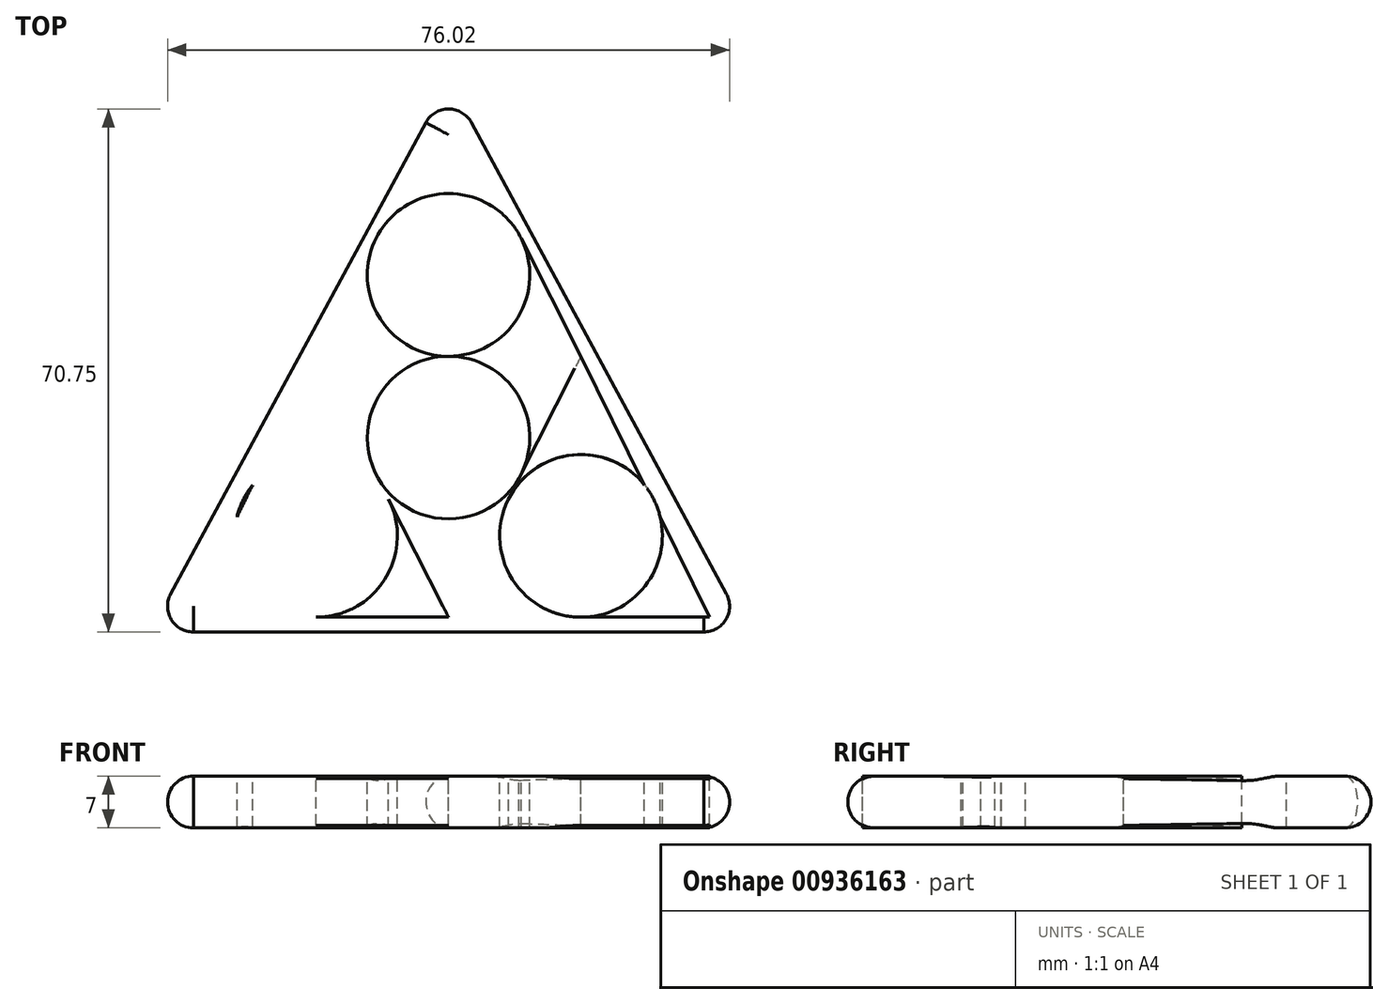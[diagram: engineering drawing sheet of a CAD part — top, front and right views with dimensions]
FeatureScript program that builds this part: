
annotation { "Feature Type Name" : "Feature", "Feature Type Description" : "" }
export const myFeature = defineFeature(function(context is Context, id is Id, definition is map)
    precondition{}
    {
        {
            var Q0;
            Q0=qCreatedBy(makeId("Top.planeOp"),FACE);
            var sketch = newSketch(context, id + "F0", { "sketchPlane" : qUnion([Q0])});
            skLineSegment(sketch, "E0", {"start": v(0, -35.3) * mm, "end": v(-17.92, 0) * mm});
            skLineSegment(sketch, "E1", {"start": v(-17.92, 0) * mm, "end": v(17.92, 0) * mm});
            skLineSegment(sketch, "E2", {"start": v(17.92, 0) * mm, "end": v(0, -35.3) * mm});
            skLineSegment(sketch, "E3", {"start": v(-17.92, 0) * mm, "end": v(-35.3, -35.3) * mm});
            skLineSegment(sketch, "E4", {"start": v(-35.3, -35.3) * mm, "end": v(0, -35.3) * mm});
            skLineSegment(sketch, "E5.MirrorCS", {"start": v(17.92, 0) * mm, "end": v(26.49, -17.4) * mm});
            skLineSegment(sketch, "E6.MirrorCS", {"start": v(35.3, -35.3) * mm, "end": v(0, -35.3) * mm});
            skLineSegment(sketch, "E7", {"start": v(-17.92, 0) * mm, "end": v(0, 35.3) * mm});
            skLineSegment(sketch, "E8", {"start": v(0, 35.3) * mm, "end": v(17.92, 0) * mm});
            skCircle(sketch, "E9", {"center": v(0, -11) * mm, "radius": 11 * mm});
            skPoint(sketch, "E9.centerSnap0", {"position": v(11, -22) * mm});
            skLineSegment(sketch, "E10", {"start": v(0, 35.3) * mm, "end": v(0, 37.3) * mm});
            skLineSegment(sketch, "E11", {"start": v(0, 37.3) * mm, "end": v(-40.39, -37.3) * mm});
            skLineSegment(sketch, "E12", {"start": v(-40.39, -37.3) * mm, "end": v(40.39, -37.3) * mm});
            skLineSegment(sketch, "E13", {"start": v(40.39, -37.3) * mm, "end": v(0, 37.3) * mm});
            skCircle(sketch, "E14", {"center": v(0, 11) * mm, "radius": 11 * mm});
            skPoint(sketch, "E15.center", {"position": v(0, 0) * mm});
            skArc(sketch, "E16.trimOffspring", {"start": v(9.51, -16.56) * mm, "mid": v(9.52, -16.53) * mm, "end": v(9.53, -16.5) * mm});
            skPoint(sketch, "E17", {"position": v(17.92, -24.3) * mm});
            skPoint(sketch, "E18", {"position": v(-17.52, -22.4) * mm});
            skCircle(sketch, "E19", {"center": v(17.92, -24.3) * mm, "radius": 11 * mm});
            skCircle(sketch, "E20.MirrorC", {"center": v(-17.92, -24.3) * mm, "radius": 11 * mm});
            skArc(sketch, "E21.trimOffspring", {"start": v(-10.18, -16.48) * mm, "mid": v(-9.86, -16.5) * mm, "end": v(-9.54, -16.5) * mm});
            skLineSegment(sketch, "E22.trimOffspring", {"start": v(28.61, -21.72) * mm, "end": v(35.3, -35.3) * mm});
            skSolve(sketch);
        }
        {
            var Q0;
            Q0=makeQuery(id+"F0.imprint","IMPRINT",FACE,{"disambiguationData":[TD([[makeQuery(id+"F0.imprint","IMPRINT",EDGE,{"derivedFrom":sQuery(id+"F0.wireOp",EDGE,"E11")}),1.0]])]});
            var Q1;
            {var subQ0=sQuery(id+"F0.wireOp",EDGE,"E8");var subQ1=sQuery(id+"F0.wireOp",EDGE,"E7");var subQ2=makeQuery(id+"F0.imprint","INTERSECT",VERTEX,{"derivedFrom":[subQ1,subQ0]});Q1=makeQuery(id+"F0.imprint","IMPRINT",FACE,{"disambiguationData":[TD([[makeQuery(id+"F0.imprint","IMPRINT",EDGE,{"disambiguationData":[TD([[subQ2,1.0]])],"derivedFrom":subQ1}),-1.0]])]});}
            var Q2;
            {var subQ0=sQuery(id+"F0.wireOp",EDGE,"E4");var subQ1=sQuery(id+"F0.wireOp",EDGE,"E3");var subQ2=makeQuery(id+"F0.imprint","INTERSECT",VERTEX,{"derivedFrom":[subQ1,subQ0]});Q2=makeQuery(id+"F0.imprint","IMPRINT",FACE,{"disambiguationData":[TD([[makeQuery(id+"F0.imprint","IMPRINT",EDGE,{"disambiguationData":[TD([[subQ2,1.0]])],"derivedFrom":subQ1}),1.0]])]});}
            var Q3;
            {var subQ0=sQuery(id+"F0.wireOp",EDGE,"E6.MirrorCS");var subQ1=sQuery(id+"F0.wireOp",EDGE,"E5.MirrorCS");var subQ2=makeQuery(id+"F0.imprint","INTERSECT",VERTEX,{"derivedFrom":[subQ1,subQ0]});Q3=makeQuery(id+"F0.imprint","IMPRINT",FACE,{"disambiguationData":[TD([[makeQuery(id+"F0.imprint","IMPRINT",EDGE,{"disambiguationData":[TD([[subQ2,1.0]])],"derivedFrom":subQ1}),-1.0]])]});}
            var Q4;
            {var subQ0=sQuery(id+"F0.wireOp",EDGE,"E7");var subQ3=sQuery(id+"F0.wireOp",EDGE,"E14");var subQ5=makeQuery(id+"F0.imprint","INTERSECT",VERTEX,{"derivedFrom":[subQ0,subQ3]});Q4=makeQuery(id+"F0.imprint","IMPRINT",FACE,{"disambiguationData":[TD([[makeQuery(id+"F0.imprint","IMPRINT",EDGE,{"disambiguationData":[TD([[subQ5,-1.0]])],"derivedFrom":subQ3}),-1.0]])]});}
            var Q5;
            {var subQ1=sQuery(id+"F0.wireOp",EDGE,"E0");var subQ3=sQuery(id+"F0.wireOp",EDGE,"E20.MirrorC");var subQ4=makeQuery(id+"F0.imprint","INTERSECT",VERTEX,{"derivedFrom":[subQ1,subQ3]});Q5=makeQuery(id+"F0.imprint","IMPRINT",FACE,{"disambiguationData":[TD([[makeQuery(id+"F0.imprint","IMPRINT",EDGE,{"disambiguationData":[TD([[subQ4,-1.0]])],"derivedFrom":subQ3}),1.0]])]});}
            var Q6;
            {var subQ1=sQuery(id+"F0.wireOp",EDGE,"E2");var subQ3=sQuery(id+"F0.wireOp",EDGE,"E19");var subQ4=makeQuery(id+"F0.imprint","INTERSECT",VERTEX,{"derivedFrom":[subQ1,subQ3]});Q6=makeQuery(id+"F0.imprint","IMPRINT",FACE,{"disambiguationData":[TD([[makeQuery(id+"F0.imprint","IMPRINT",EDGE,{"disambiguationData":[TD([[subQ4,-1.0]])],"derivedFrom":subQ3}),-1.0]])]});}
            var Q7;
            {var subQ0=sQuery(id+"F0.wireOp",EDGE,"E21.trimOffspring");Q7=makeQuery(id+"F0.imprint","IMPRINT",FACE,{"disambiguationData":[TD([[makeQuery(id+"F0.imprint","IMPRINT",EDGE,{"derivedFrom":subQ0}),1.0]])]});}
            var Q8;
            {var subQ0=sQuery(id+"F0.wireOp",EDGE,"E21.trimOffspring");Q8=makeQuery(id+"F0.imprint","IMPRINT",FACE,{"disambiguationData":[TD([[makeQuery(id+"F0.imprint","IMPRINT",EDGE,{"derivedFrom":subQ0}),-1.0]])]});}
            var Q9;
            {var subQ0=sQuery(id+"F0.wireOp",EDGE,"E16.trimOffspring");Q9=makeQuery(id+"F0.imprint","IMPRINT",FACE,{"disambiguationData":[TD([[makeQuery(id+"F0.imprint","IMPRINT",EDGE,{"derivedFrom":subQ0}),1.0]])]});}
            var Q10;
            {var subQ1=sQuery(id+"F0.wireOp",EDGE,"E0");var subQ3=sQuery(id+"F0.wireOp",EDGE,"E9");var subQ4=makeQuery(id+"F0.imprint","INTERSECT",VERTEX,{"derivedFrom":[subQ1,subQ3]});Q10=makeQuery(id+"F0.imprint","IMPRINT",FACE,{"disambiguationData":[TD([[makeQuery(id+"F0.imprint","IMPRINT",EDGE,{"disambiguationData":[TD([[subQ4,1.0]])],"derivedFrom":subQ3}),-1.0]])]});}
            var Q11;
            {var subQ1=sQuery(id+"F0.wireOp",EDGE,"E2");var subQ5=makeQuery(id+"F0.imprint","INTERSECT",VERTEX,{"derivedFrom":[subQ1,sQuery(id+"F0.wireOp",EDGE,"E16.trimOffspring")]});Q11=makeQuery(id+"F0.imprint","IMPRINT",FACE,{"disambiguationData":[TD([[makeQuery(id+"F0.imprint","IMPRINT",EDGE,{"disambiguationData":[TD([[subQ5,1.0]])],"derivedFrom":subQ1}),1.0]])]});}
            extrude(context, id + "F1", {"entities" : qUnion([Q0, Q1, Q2, Q3, Q4, Q5, Q6, Q7, Q8, Q9, Q10, Q11]), "oppositeDirection" : true, "depth" : 7 * mm, "offsetDistance" : 25 * mm});
        }
        {
            var Q0;
            {var subQ0=sQuery(id+"F0.wireOp",EDGE,"E8");var subQ3=sQuery(id+"F0.wireOp",EDGE,"E14");var subQ5=makeQuery(id+"F0.imprint","INTERSECT",VERTEX,{"derivedFrom":[subQ0,subQ3]});Q0=makeQuery(id+"F0.imprint","IMPRINT",FACE,{"disambiguationData":[TD([[makeQuery(id+"F0.imprint","IMPRINT",EDGE,{"disambiguationData":[TD([[subQ5,1.0]])],"derivedFrom":subQ3}),-1.0]])]});}
            var Q1;
            {var subQ1=sQuery(id+"F0.wireOp",EDGE,"E2");var subQ5=makeQuery(id+"F0.imprint","INTERSECT",VERTEX,{"derivedFrom":[subQ1,sQuery(id+"F0.wireOp",EDGE,"E16.trimOffspring")]});Q1=makeQuery(id+"F0.imprint","IMPRINT",FACE,{"disambiguationData":[TD([[makeQuery(id+"F0.imprint","IMPRINT",EDGE,{"disambiguationData":[TD([[subQ5,1.0]])],"derivedFrom":subQ1}),1.0]])]});}
            var Q2;
            {var subQ0=sQuery(id+"F0.wireOp",EDGE,"E2");var subQ3=sQuery(id+"F0.wireOp",EDGE,"E9");var subQ5=makeQuery(id+"F0.imprint","INTERSECT",VERTEX,{"derivedFrom":[subQ0,subQ3]});Q2=makeQuery(id+"F0.imprint","IMPRINT",FACE,{"disambiguationData":[TD([[makeQuery(id+"F0.imprint","IMPRINT",EDGE,{"disambiguationData":[TD([[subQ5,-1.0]])],"derivedFrom":subQ3}),-1.0]])]});}
            var Q3;
            {var subQ0=sQuery(id+"F0.wireOp",EDGE,"E22.trimOffspring");Q3=makeQuery(id+"F0.imprint","IMPRINT",FACE,{"disambiguationData":[TD([[makeQuery(id+"F0.imprint","IMPRINT",EDGE,{"derivedFrom":subQ0}),-1.0]])]});}
            extrude(context, id + "F2", {"entities" : qUnion([Q0, Q1, Q2, Q3]), "oppositeDirection" : true, "depth" : 7 * mm, "offsetDistance" : 25 * mm});
        }
        {
            var Q0;
            Q0=makeQuery(id+"F1.opExtrude","CAP_EDGE",EDGE,{"disambiguationData":[OSD([sQuery(id+"F0.wireOp",EDGE,"E12")])],"isStart":true});
            var Q1;
            Q1=makeQuery(id+"F1.opExtrude","CAP_EDGE",EDGE,{"disambiguationData":[OSD([sQuery(id+"F0.wireOp",EDGE,"E12")])],"isStart":false});
            fillet(context, id + "F3", {"entities" : qUnion([Q0, Q1]), "radius" : 3.5 * mm, "tangentPropagation" : true, "allowEdgeOverflow" : false});
        }
        {
            var Q0;
            Q0=makeQuery(id+"F1.opExtrude","CAP_EDGE",EDGE,{"disambiguationData":[OSD([sQuery(id+"F0.wireOp",EDGE,"E11")])],"isStart":true});
            var Q1;
            Q1=makeQuery(id+"F1.opExtrude","CAP_EDGE",EDGE,{"disambiguationData":[OSD([sQuery(id+"F0.wireOp",EDGE,"E11")])],"isStart":false});
            fillet(context, id + "F4", {"entities" : qUnion([Q0, Q1]), "radius" : 3.5 * mm, "tangentPropagation" : true, "allowEdgeOverflow" : false});
        }
        {
            var Q0;
            Q0=makeQuery(id+"F1.opExtrude","CAP_EDGE",EDGE,{"disambiguationData":[OSD([sQuery(id+"F0.wireOp",EDGE,"E13")])],"isStart":true});
            var Q1;
            Q1=makeQuery(id+"F1.opExtrude","CAP_EDGE",EDGE,{"disambiguationData":[OSD([sQuery(id+"F0.wireOp",EDGE,"E13")])],"isStart":false});
            fillet(context, id + "F5", {"entities" : qUnion([Q0, Q1]), "radius" : 3.5 * mm, "tangentPropagation" : true, "allowEdgeOverflow" : false});
        }
    });
